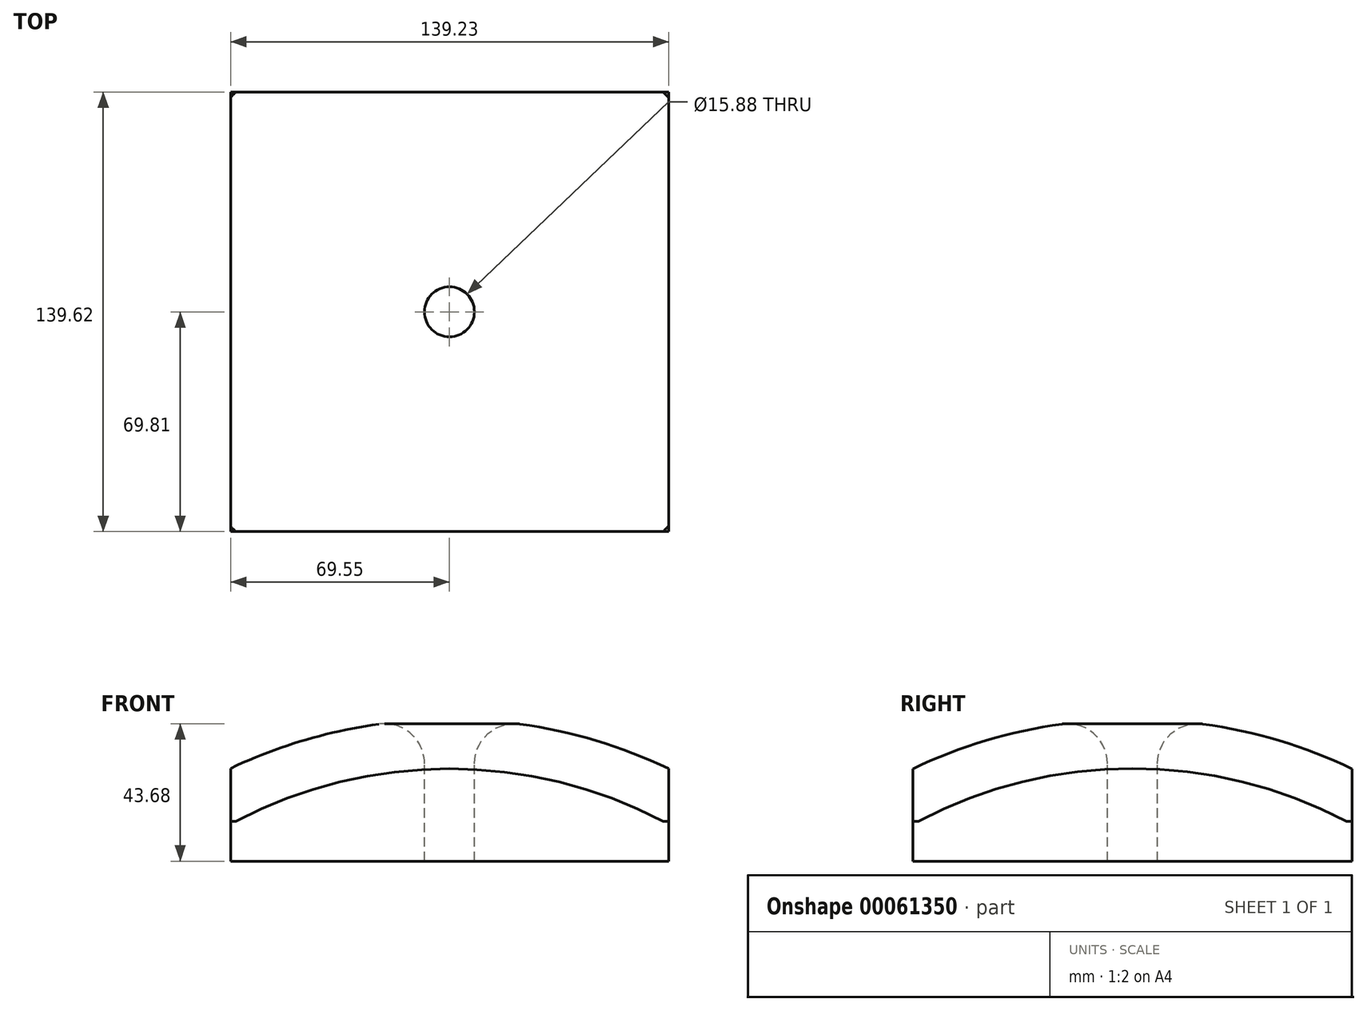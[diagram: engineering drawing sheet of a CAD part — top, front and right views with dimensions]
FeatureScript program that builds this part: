
annotation { "Feature Type Name" : "Feature", "Feature Type Description" : "" }
export const myFeature = defineFeature(function(context is Context, id is Id, definition is map)
    precondition{}
    {
        {
            var Q0;
            Q0=qCreatedBy(makeId("Top.planeOp"),FACE);
            var sketch = newSketch(context, id + "F0", { "sketchPlane" : qUnion([Q0])});
            skLineSegment(sketch, "E0.rect.bottom", {"start": v(69.85, -69.85) * mm, "end": v(-69.85, -69.85) * mm});
            skLineSegment(sketch, "E0.rect.top", {"start": v(69.85, 69.85) * mm, "end": v(-69.85, 69.85) * mm});
            skLineSegment(sketch, "E0.rect.left", {"start": v(69.85, -69.85) * mm, "end": v(69.85, 69.85) * mm});
            skLineSegment(sketch, "E0.rect.right", {"start": v(-69.85, -69.85) * mm, "end": v(-69.85, 69.85) * mm});
            skPoint(sketch, "E0.rect.middle", {"position": v(0, 0) * mm});
            skCircle(sketch, "E1", {"center": v(0, 0) * mm, "radius": 98.78 * mm, "construction": true});
            skCircle(sketch, "E2", {"center": v(0, 0) * mm, "radius": 7.94 * mm});
            skSolve(sketch);
        }
        {
            var Q0;
            Q0=makeQuery(id+"F0.imprint","IMPRINT",FACE,{"disambiguationData":[TD([[makeQuery(id+"F0.imprint","IMPRINT",EDGE,{"derivedFrom":sQuery(id+"F0.wireOp",EDGE,"E0.rect.bottom")}),-1.0]])]});
            extrude(context, id + "F1", {"entities" : qUnion([Q0]), "depth" : 12.7 * mm});
        }
        {
            var Q0;
            Q0=qCreatedBy(makeId("Front.planeOp"),FACE);
            var sketch = newSketch(context, id + "F2", { "sketchPlane" : qUnion([Q0])});
            skArc(sketch, "E3", {"start": v(0, 45.1) * mm, "mid": v(-60.54, 33.41) * mm, "end": v(-112.37, 0) * mm});
            skLineSegment(sketch, "E4", {"start": v(-112.37, 0) * mm, "end": v(0, 0) * mm});
            skLineSegment(sketch, "E5", {"start": v(0, 45.1) * mm, "end": v(0, 0) * mm});
            skSolve(sketch);
        }
        {
            var Q0;
            Q0=makeQuery(id+"F2.imprint","IMPRINT",FACE,{"disambiguationData":[TD([[makeQuery(id+"F2.imprint","IMPRINT",EDGE,{"derivedFrom":sQuery(id+"F2.wireOp",EDGE,"E3")}),1.0]])]});
            var Q1;
            Q1 = qSketchRegion(id + "F4", true);
            var Q2;
            Q2=sQuery(id+"F2.wireOp",EDGE,"E5");
            revolve(context, id + "F3", {"operationType" : NewBodyOperationType.ADD, "entities" : qUnion([Q0, Q1]), "axis" : qUnion([Q2]), "revolveType" : RevolveType.FULL});
        }
        {
            var Q0;
            Q0=qCreatedBy(makeId("Front.planeOp"),FACE);
            var sketch = newSketch(context, id + "F4", { "sketchPlane" : qUnion([Q0])});
            skLineSegment(sketch, "E6", {"start": v(69.68, 1) * mm, "end": v(69.68, -26.36) * mm, "construction": true});
            skLineSegment(sketch, "E7.bottom", {"start": v(69.68, -12.68) * mm, "end": v(126.31, -12.68) * mm});
            skLineSegment(sketch, "E7.top", {"start": v(69.68, 49.5) * mm, "end": v(126.31, 49.5) * mm});
            skLineSegment(sketch, "E7.left", {"start": v(69.68, -12.68) * mm, "end": v(69.68, 49.5) * mm});
            skLineSegment(sketch, "E7.right", {"start": v(126.31, -12.68) * mm, "end": v(126.31, 49.5) * mm});
            skLineSegment(sketch, "E8", {"start": v(-69.55, 11.43) * mm, "end": v(-69.55, -30.11) * mm, "construction": true});
            skLineSegment(sketch, "E9", {"start": v(-68.58, -30.11) * mm, "end": v(-69.55, -30.11) * mm, "construction": true});
            skLineSegment(sketch, "E10.bottom", {"start": v(-69.55, -11.92) * mm, "end": v(-129.25, -11.92) * mm});
            skLineSegment(sketch, "E10.top", {"start": v(-69.55, 51.43) * mm, "end": v(-129.25, 51.43) * mm});
            skLineSegment(sketch, "E10.left", {"start": v(-69.55, -11.92) * mm, "end": v(-69.55, 51.43) * mm});
            skLineSegment(sketch, "E10.right", {"start": v(-129.25, -11.92) * mm, "end": v(-129.25, 51.43) * mm});
            skSolve(sketch);
        }
        {
            var Q0;
            Q0=makeQuery(id+"F4.imprint","IMPRINT",FACE,{"disambiguationData":[TD([[makeQuery(id+"F4.imprint","IMPRINT",EDGE,{"derivedFrom":sQuery(id+"F4.wireOp",EDGE,"E10.bottom")}),-1.0]])]});
            var Q1;
            Q1=makeQuery(id+"F4.imprint","IMPRINT",FACE,{"disambiguationData":[TD([[makeQuery(id+"F4.imprint","IMPRINT",EDGE,{"derivedFrom":sQuery(id+"F4.wireOp",EDGE,"E7.bottom")}),1.0]])]});
            extrude(context, id + "F5", {"entities" : qUnion([Q0, Q1]), "operationType" : NewBodyOperationType.REMOVE, "endBound" : BoundingType.SYMMETRIC, "oppositeDirection" : true, "depth" : 203.2 * mm});
        }
        {
            var Q0;
            Q0=qCreatedBy(makeId("Right.planeOp"),FACE);
            var sketch = newSketch(context, id + "F6", { "sketchPlane" : qUnion([Q0])});
            skLineSegment(sketch, "E11", {"start": v(69.8, 8.48) * mm, "end": v(69.8, -30.36) * mm, "construction": true});
            skLineSegment(sketch, "E12", {"start": v(-69.8, 10.7) * mm, "end": v(-69.8, -22.5) * mm, "construction": true});
            skLineSegment(sketch, "E13.bottom", {"start": v(-69.8, -8.73) * mm, "end": v(-117.04, -8.73) * mm});
            skLineSegment(sketch, "E13.top", {"start": v(-69.8, 30.6) * mm, "end": v(-117.04, 30.6) * mm});
            skLineSegment(sketch, "E13.left", {"start": v(-69.8, -8.73) * mm, "end": v(-69.8, 30.6) * mm});
            skLineSegment(sketch, "E13.right", {"start": v(-117.04, -8.73) * mm, "end": v(-117.04, 30.6) * mm});
            skLineSegment(sketch, "E14.bottom", {"start": v(69.8, -10.94) * mm, "end": v(115.9, -10.94) * mm});
            skLineSegment(sketch, "E14.top", {"start": v(69.8, 30.6) * mm, "end": v(115.9, 30.6) * mm});
            skLineSegment(sketch, "E14.left", {"start": v(69.8, -10.94) * mm, "end": v(69.8, 30.6) * mm});
            skLineSegment(sketch, "E14.right", {"start": v(115.9, -10.94) * mm, "end": v(115.9, 30.6) * mm});
            skSolve(sketch);
        }
        {
            var Q0;
            Q0=makeQuery(id+"F6.imprint","IMPRINT",FACE,{"disambiguationData":[TD([[makeQuery(id+"F6.imprint","IMPRINT",EDGE,{"derivedFrom":sQuery(id+"F6.wireOp",EDGE,"E13.bottom")}),-1.0]])]});
            var Q1;
            Q1=makeQuery(id+"F6.imprint","IMPRINT",FACE,{"disambiguationData":[TD([[makeQuery(id+"F6.imprint","IMPRINT",EDGE,{"derivedFrom":sQuery(id+"F6.wireOp",EDGE,"E14.bottom")}),1.0]])]});
            extrude(context, id + "F7", {"entities" : qUnion([Q0, Q1]), "operationType" : NewBodyOperationType.REMOVE, "endBound" : BoundingType.SYMMETRIC, "oppositeDirection" : true, "depth" : 203.2 * mm});
        }
        {
            var Q0;
            Q0=qCreatedBy(makeId("Top.planeOp"),FACE);
            var sketch = newSketch(context, id + "F8", { "sketchPlane" : qUnion([Q0])});
            skCircle(sketch, "E15", {"center": v(0, 0) * mm, "radius": 7.94 * mm});
            skSolve(sketch);
        }
        {
            var Q0;
            Q0=makeQuery(id+"F0.imprint","IMPRINT",FACE,{"disambiguationData":[TD([[makeQuery(id+"F0.imprint","IMPRINT",EDGE,{"derivedFrom":sQuery(id+"F0.wireOp",EDGE,"E2")}),1.0]])]});
            var Q1;
            Q1=sQuery(id+"F8.wireOp",EDGE,"E15");
            extrude(context, id + "F9", {"entities" : qUnion([Q0]), "operationType" : NewBodyOperationType.REMOVE, "surfaceEntities" : qUnion([Q1]), "endBound" : BoundingType.SYMMETRIC, "oppositeDirection" : true, "depth" : 152.4 * mm});
        }
        {
            var Q0;
            Q0=makeQuery(id+"F9.boolean.opBoolean","INTERSECT",EDGE,{"derivedFrom":[makeQuery(id+"F3.opRevolve","SWEPT_FACE",FACE,{"disambiguationData":[OSD([sQuery(id+"F2.wireOp",EDGE,"E3")])]}),makeQuery(id+"F9.opExtrude","SWEPT_FACE",FACE,{"disambiguationData":[OSD([sQuery(id+"F0.wireOp",EDGE,"E2")])]})]});
            fillet(context, id + "F10", {"entities" : qUnion([Q0]), "radius" : 12.7 * mm, "tangentPropagation" : true, "allowEdgeOverflow" : false});
        }
    });
